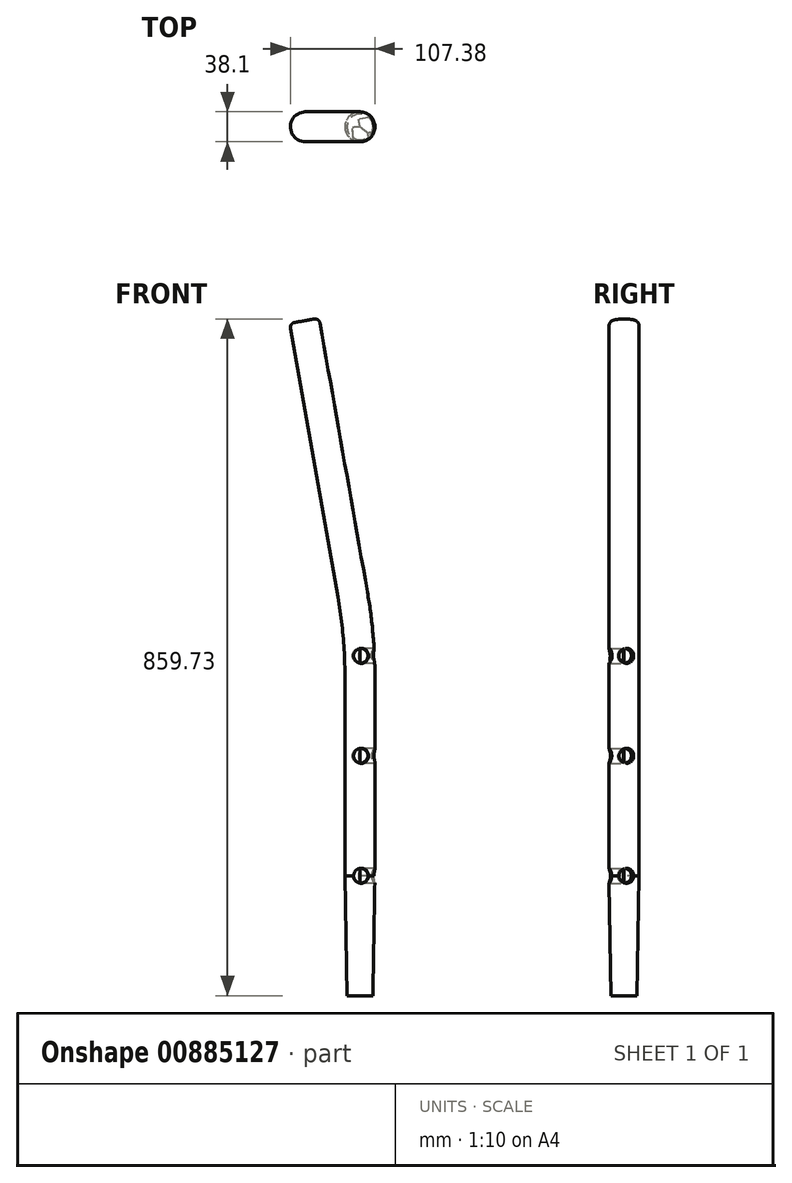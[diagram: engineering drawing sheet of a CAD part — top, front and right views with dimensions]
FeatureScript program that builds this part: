
annotation { "Feature Type Name" : "Feature", "Feature Type Description" : "" }
export const myFeature = defineFeature(function(context is Context, id is Id, definition is map)
    precondition{}
    {
        {
            var Q0;
            Q0=qCreatedBy(makeId("Front.planeOp"),FACE);
            var sketch = newSketch(context, id + "F0", { "sketchPlane" : qUnion([Q0])});
            skLineSegment(sketch, "E0", {"start": v(0, 0) * mm, "end": v(0, 403.87) * mm});
            skLineSegment(sketch, "E1", {"start": v(0, 457.2) * mm, "end": v(0, 457.2) * mm});
            skLineSegment(sketch, "E2", {"start": v(-9.26, 509.72) * mm, "end": v(-70.57, 857.43) * mm});
            skPoint(sketch, "E3.visualSharp", {"position": v(0, 457.2) * mm});
            skArc(sketch, "E3.filletArc", {"start": v(0, 403.87) * mm, "mid": v(-2.32, 457) * mm, "end": v(-9.26, 509.72) * mm});
            skSolve(sketch);
        }
        {
            var Q0;
            Q0=qCreatedBy(makeId("Top.planeOp"),FACE);
            var sketch = newSketch(context, id + "F1", { "sketchPlane" : qUnion([Q0])});
            skCircle(sketch, "E4", {"center": v(0, 0) * mm, "radius": 19.05 * mm});
            skSolve(sketch);
        }
        {
            var Q0;
            Q0 = qSketchRegion(id + "F1", true);
            var Q1;
            Q1 = qBodyType(qCreatedBy(id + "F0" ,EDGE), BodyType.WIRE);
            sweep(context, id + "F2", {"profiles" : qUnion([Q0]), "path" : qUnion([Q1])});
        }
        {
            var Q0;
            Q0=makeQuery(id+"F2.opSweep","CAP_EDGE",EDGE,{"disambiguationData":[OSD([sQuery(id+"F0.wireOp",VERTEX,"E2.end"),sQuery(id+"F1.wireOp",EDGE,"E4")])],"isStart":false});
            fillet(context, id + "F3", {"entities" : qUnion([Q0]), "radius" : 6.35 * mm, "tangentPropagation" : true, "allowEdgeOverflow" : false});
        }
        {
            var Q0;
            Q0=makeQuery(id+"F2.opSweep","CAP_EDGE",EDGE,{"disambiguationData":[OSD([sQuery(id+"F0.wireOp",VERTEX,"E0.start"),sQuery(id+"F1.wireOp",EDGE,"E4")])],"isStart":true});
            chamfer(context, id + "F4", {"entities" : qUnion([Q0]), "chamferType" : ChamferType.OFFSET_ANGLE, "width" : 152.4 * mm, "oppositeDirection" : false, "angle" : 1 * degree, "tangentPropagation" : true});
        }
        {
            var Q0;
            Q0=makeQuery(id+"F2.opSweep","SWEPT_FACE",FACE,{"disambiguationData":[OSD([sQuery(id+"F0.wireOp",EDGE,"E0"),sQuery(id+"F1.wireOp",EDGE,"E4")])]});
            cPlane(context, id + "F5", {"entities" : qUnion([Q0]), "cplaneType" : CPlaneType.LINE_ANGLE, "offset" : 25.4 * mm, "angle" : 10 * degree, "width" : 152.4 * mm, "height" : 152.4 * mm});
        }
        {
            var Q0;
            Q0=qCreatedBy(id+"F5.planeOp",FACE);
            var sketch = newSketch(context, id + "F6", { "sketchPlane" : qUnion([Q0])});
            skPoint(sketch, "E5", {"position": v(0, 152.4) * mm});
            skPoint(sketch, "E6", {"position": v(0, 304.8) * mm});
            skPoint(sketch, "E7", {"position": v(0, 431.8) * mm});
            skSolve(sketch);
        }
        {
            var Q0;
            Q0=sQuery(id+"F6.wireOp",VERTEX,"E7");
            var Q1;
            Q1=sQuery(id+"F6.wireOp",VERTEX,"E6");
            var Q2;
            Q2=sQuery(id+"F6.wireOp",VERTEX,"E5");
            var Q3;
            Q3=makeQuery(id+"F2.opSweep","SWEPT_BODY",BODY,{"disambiguationData":[OSD([sQuery(id+"F0.wireOp",EDGE,"E2"),sQuery(id+"F1.wireOp",EDGE,"E4")])]});
            hole(context, id + "F7", {"style" : HoleStyle.SIMPLE, "endStyle" : HoleEndStyle.THROUGH, "oppositeDirection" : true, "holeDiameter" : 19.05 * mm, "majorDiameter" : 6.35 * mm, "isTappedThrough" : true, "tappedDepth" : 12.7 * mm, "tapClearance" : 3, "locations" : qUnion([Q0, Q1, Q2]), "scope" : qUnion([Q3])});
        }
        {
            var Q0;
            Q0=makeQuery(id+"F2.opSweep","SWEPT_FACE",FACE,{"disambiguationData":[OSD([sQuery(id+"F0.wireOp",EDGE,"E0"),sQuery(id+"F1.wireOp",EDGE,"E4")])]});
            cPlane(context, id + "F8", {"entities" : qUnion([Q0]), "cplaneType" : CPlaneType.LINE_ANGLE, "offset" : 25.4 * mm, "angle" : 85 * degree, "oppositeDirection" : true, "width" : 152.4 * mm, "height" : 152.4 * mm});
        }
        {
            var Q0;
            Q0=qCreatedBy(id+"F8.planeOp",FACE);
            var sketch = newSketch(context, id + "F9", { "sketchPlane" : qUnion([Q0])});
            skPoint(sketch, "E8", {"position": v(0, 152.4) * mm});
            skPoint(sketch, "E9", {"position": v(0, 304.8) * mm});
            skPoint(sketch, "E10", {"position": v(0, 431.8) * mm});
            skSolve(sketch);
        }
        {
            var Q0;
            Q0=sQuery(id+"F9.wireOp",VERTEX,"E10");
            var Q1;
            Q1=sQuery(id+"F9.wireOp",VERTEX,"E8");
            var Q2;
            Q2=sQuery(id+"F9.wireOp",VERTEX,"E9");
            var Q3;
            Q3=makeQuery(id+"F2.opSweep","SWEPT_BODY",BODY,{"disambiguationData":[OSD([sQuery(id+"F0.wireOp",EDGE,"E2"),sQuery(id+"F1.wireOp",EDGE,"E4")])]});
            hole(context, id + "F10", {"style" : HoleStyle.SIMPLE, "endStyle" : HoleEndStyle.THROUGH, "oppositeDirection" : true, "holeDiameter" : 19.05 * mm, "majorDiameter" : 6.35 * mm, "isTappedThrough" : true, "tappedDepth" : 12.7 * mm, "tapClearance" : 3, "locations" : qUnion([Q0, Q1, Q2]), "scope" : qUnion([Q3])});
        }
    });
